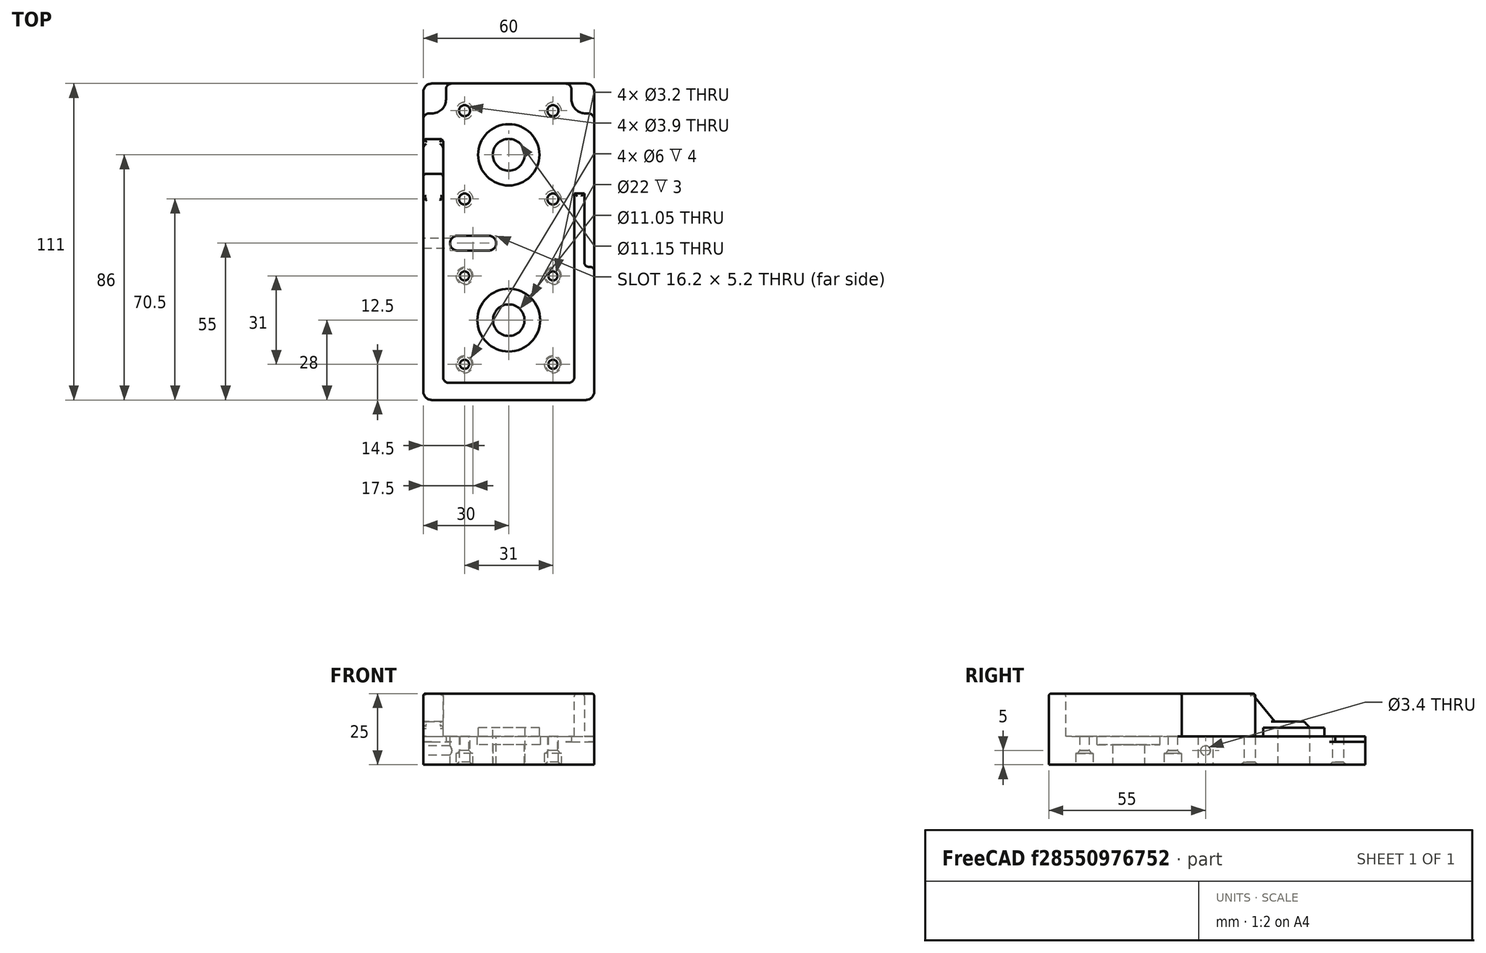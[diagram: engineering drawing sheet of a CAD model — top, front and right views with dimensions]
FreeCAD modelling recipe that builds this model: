
FCSTD DOCUMENT  (FreeCAD 0.19R)
Label: BeltDriveUnit2
License: All rights reserved
LicenseURL: http://en.wikipedia.org/wiki/All_rights_reserved
objects: Sketcher::SketchObject×11, PartDesign::Fillet×9, PartDesign::Pocket×8, PartDesign::Pad×3, PartDesign::Chamfer×3, PartDesign::Body×1, Mesh::Feature×1
note: 58 computed .brp shape members not serialized (recipe doc carries the construction recipe); baked Part::Feature solids carry a one-line shape summary decoded from their .brp

FEATURE [Sketcher::SketchObject] Sketch
  FullyConstrained = true
  MapMode = 5
  Support = -> [XY_Plane]
  sketch-geometry (17):
    g0: LineSegment StartX=-30 StartY=25 StartZ=0 EndX=30 EndY=25 EndZ=0
    g1: LineSegment StartX=30 StartY=25 StartZ=0 EndX=30 EndY=-86 EndZ=0
    g2: LineSegment StartX=30 StartY=-86 StartZ=0 EndX=-30 EndY=-86 EndZ=0
    g3: LineSegment StartX=-30 StartY=-86 StartZ=0 EndX=-30 EndY=25 EndZ=0
    g4: LineSegment StartX=-21 StartY=21 StartZ=0 EndX=21 EndY=21 EndZ=0
    g5: LineSegment StartX=21 StartY=21 StartZ=0 EndX=21 EndY=-21 EndZ=0
    g6: LineSegment StartX=21 StartY=-21 StartZ=0 EndX=-21 EndY=-21 EndZ=0
    g7: LineSegment StartX=-21 StartY=-21 StartZ=0 EndX=-21 EndY=21 EndZ=0
    g8: Circle CenterX=-15.5 CenterY=15.5 CenterZ=0 NormalX=0 NormalY=0 NormalZ=1 AngleXU=0 Radius=1.95
    g9: Circle CenterX=15.5 CenterY=15.5 CenterZ=0 NormalX=0 NormalY=0 NormalZ=1 AngleXU=0 Radius=1.95
    g10: Circle CenterX=-15.5 CenterY=-15.5 CenterZ=0 NormalX=0 NormalY=0 NormalZ=1 AngleXU=0 Radius=1.95
    g11: Circle CenterX=15.5 CenterY=-15.5 CenterZ=0 NormalX=0 NormalY=0 NormalZ=1 AngleXU=0 Radius=1.95
    g12: Circle CenterX=0 CenterY=-58 CenterZ=0 NormalX=0 NormalY=0 NormalZ=1 AngleXU=0 Radius=5.525
    g13: Circle CenterX=-15.5 CenterY=-42.5 CenterZ=0 NormalX=0 NormalY=0 NormalZ=1 AngleXU=0 Radius=1.6
    g14: Circle CenterX=15.5 CenterY=-42.5 CenterZ=0 NormalX=0 NormalY=0 NormalZ=1 AngleXU=0 Radius=1.6
    g15: Circle CenterX=-15.5 CenterY=-73.5 CenterZ=0 NormalX=0 NormalY=0 NormalZ=1 AngleXU=0 Radius=1.6
    g16: Circle CenterX=15.5 CenterY=-73.5 CenterZ=0 NormalX=0 NormalY=0 NormalZ=1 AngleXU=0 Radius=1.6
  constraints (44):
    c: Coincident(g0,g1)
    c: Coincident(g1,g2)
    c: Coincident(g2,g3)
    c: Coincident(g3,g0)
    c: Horizontal(g2)
    c: Vertical(g1)
    c: Vertical(g3)
    c: Coincident(g4,g5)
    c: Coincident(g5,g6)
    c: Coincident(g6,g7)
    c: Coincident(g7,g4)
    c: Horizontal(g4)
    c: Horizontal(g6)
    c: Vertical(g5)
    c: Vertical(g7)
    c: Equal(g5,g4)
    c: Distance(g5) = 42
    c: Symmetric(g4,g6,g-1)
    c: Symmetric(g0,g0,g-2)
    c: Distance(g4,g0) = 4
    c: Distance(g0) = 60
    c: Diameter(g11) = 3.9
    c: Equal(g11,g10)
    c: Equal(g11,g8)
    c: Equal(g11,g9)
    c: Distance(g9,g8) = 31
    c: Symmetric(g9,g8,g-2)
    c: Distance(g10,g8) = 31
    c: DistanceY(g11,g9) = 31
    c: DistanceX(g10,g11) = 31
    c: Symmetric(g9,g10,g-1)
    c: Diameter(g16) = 3.2
    c: Equal(g16,g14)
    c: Equal(g16,g13)
    c: Equal(g16,g15)
    c: Symmetric(g14,g13,g-2)
    c: Symmetric(g16,g15,g-2)
    c: Symmetric(g16,g13,g12)
    c: PointOnObject(g12,g-2)
    c: Distance(g14,g13) = 31
    c: Distance(g16,g14) = 31
    c: Distance(g-1,g12) = 58
    c: Diameter(g12) = 11.05
    c: DistanceY(g1) = -86
FEATURE [PartDesign::Pad] Pad
  Direction = (1,1,1)
  Length = 10
  Length2 = 100
  Profile = -> Sketch
  Type = 0
FEATURE [Sketcher::SketchObject] Sketch004
  FullyConstrained = true
  MapMode = 5
  Placement = pos=(0,0,10) rot=(0,0,1;0rad)
  Support = -> [Pad]
  sketch-geometry (1):
    g0: Circle CenterX=0 CenterY=0 CenterZ=0 NormalX=0 NormalY=0 NormalZ=1 AngleXU=0 Radius=10.75
  constraints (2):
    c: Coincident(g0,g-1)
    c: Diameter(g0) = 21.5
FEATURE [PartDesign::Pad] Pad001
  BaseFeature = -> Pad
  Direction = (1,1,1)
  Length = 3
  Length2 = 100
  Profile = -> Sketch004
  Type = 0
FEATURE [Sketcher::SketchObject] Sketch003
  FullyConstrained = false
  MapMode = 5
  Placement = pos=(0,0,13) rot=(0,0,1;0rad)
  Support = -> [Pad001]
  sketch-geometry (1):
    g0: Circle CenterX=0 CenterY=0 CenterZ=0 NormalX=0 NormalY=0 NormalZ=1 AngleXU=0 Radius=5.575
  constraints (1):
    c: Diameter(g0) = 11.15
FEATURE [PartDesign::Pocket] Pocket
  BaseFeature = -> Pad001
  Length = 5
  Length2 = 100
  Profile = -> Sketch003
  Type = 1
FEATURE [Sketcher::SketchObject] Sketch006
  ExternalGeometry = -> [Pocket]
  FullyConstrained = true
  MapMode = 5
  Placement = pos=(0,0,10) rot=(0,0,1;0rad)
  Support = -> [Pocket]
  sketch-geometry (1):
    g0: Circle CenterX=0 CenterY=-58 CenterZ=0 NormalX=0 NormalY=0 NormalZ=1 AngleXU=0 Radius=11
  constraints (2):
    c: Coincident(g0,g-3)
    c: Diameter(g0) = 22
FEATURE [PartDesign::Pocket] Pocket001
  BaseFeature = -> Pocket
  Length = 3
  Length2 = 100
  Profile = -> Sketch006
  Type = 0
FEATURE [Sketcher::SketchObject] Sketch007
  ExternalGeometry = -> [Pocket001]
  FullyConstrained = true
  MapMode = 5
  Placement = pos=(0,0,0) rot=(1,0,0;3.14159rad)
  Support = -> [Pocket001]
  sketch-geometry (4):
    g0: Circle CenterX=-15.5 CenterY=73.5 CenterZ=0 NormalX=0 NormalY=0 NormalZ=1 AngleXU=0 Radius=3
    g1: Circle CenterX=15.5 CenterY=73.5 CenterZ=0 NormalX=0 NormalY=0 NormalZ=1 AngleXU=0 Radius=3
    g2: Circle CenterX=15.5 CenterY=42.5 CenterZ=0 NormalX=0 NormalY=0 NormalZ=1 AngleXU=0 Radius=3
    g3: Circle CenterX=-15.5 CenterY=42.5 CenterZ=0 NormalX=0 NormalY=0 NormalZ=1 AngleXU=0 Radius=3
  constraints (9):
    c: Diameter(g3) = 6
    c: Equal(g3,g1)
    c: Equal(g3,g2)
    c: Equal(g3,g0)
    c: Symmetric(g0,g2,g-3)
    c: Symmetric(g1,g3,g-3)
    c: Distance(g2,g1) = 31
    c: Distance(g3,g2) = 31
    c: Symmetric(g3,g2,g-2)
FEATURE [PartDesign::Pocket] Pocket002
  BaseFeature = -> Pocket001
  Length = 4
  Length2 = 100
  Profile = -> Sketch007
  Type = 0
FEATURE [Sketcher::SketchObject] Sketch008  label="Slot"
  ExternalGeometry = -> [Pocket002]
  FullyConstrained = true
  MapMode = 5
  Placement = pos=(0,0,10) rot=(0,0,1;0rad)
  Support = -> [Pocket002]
  sketch-geometry (11):
    g0: Circle CenterX=0 CenterY=0 CenterZ=0 NormalX=0 NormalY=0 NormalZ=1 AngleXU=0 Radius=18.5
    g1: Circle CenterX=0 CenterY=-58 CenterZ=0 NormalX=0 NormalY=0 NormalZ=1 AngleXU=0 Radius=6
    g2: LineSegment StartX=-18.0653 StartY=-3.98707 StartZ=0 EndX=-5.859 EndY=-59.2931 EndZ=0
    g3: ArcOfCircle CenterX=-18 CenterY=-31 CenterZ=0 NormalX=0 NormalY=0 NormalZ=1 AngleXU=0 Radius=2.6 StartAngle=1.5708 EndAngle=4.71239
    g4: ArcOfCircle CenterX=-7 CenterY=-31 CenterZ=0 NormalX=0 NormalY=0 NormalZ=1 AngleXU=0 Radius=2.6 StartAngle=4.71239 EndAngle=7.85398
    g5: LineSegment StartX=-18 StartY=-33.6 StartZ=0 EndX=-7 EndY=-33.6 EndZ=0
    g6: LineSegment StartX=-18 StartY=-28.4 StartZ=0 EndX=-7 EndY=-28.4 EndZ=0
    g7: Circle CenterX=-18 CenterY=-31 CenterZ=0 NormalX=0 NormalY=0 NormalZ=1 AngleXU=0 Radius=6
    g8: Circle CenterX=-7 CenterY=-31 CenterZ=0 NormalX=0 NormalY=0 NormalZ=1 AngleXU=0 Radius=6
    g9: LineSegment StartX=-15.5 StartY=-37 StartZ=0 EndX=-15.5 EndY=-79 EndZ=0
    g10: LineSegment StartX=-15.5 StartY=-31 StartZ=0 EndX=-15.5 EndY=-37 EndZ=0
  constraints (29):
    c: Diameter(g0) = 37
    c: Coincident(g0,g-1)
    c: Diameter(g1) = 12
    c: Coincident(g1,g-3)
    c: PointOnObject(g2,g0)
    c: PointOnObject(g2,g1)
    c: Tangent(g2,g0)
    c: Tangent(g1,g2)
    c: Tangent(g3,g6) = 1.5708
    c: Tangent(g3,g5) = -1.5708
    c: Tangent(g5,g4) = -1.5708
    c: Tangent(g6,g4) = 1.5708
    c: Horizontal(g5)
    c: Equal(g3,g4)
    c: Diameter(g7) = 12
    c: Coincident(g3,g7)
    c: Diameter(g8) = 12
    c: Coincident(g8,g4)
    c: Distance(g3,g3) = 5.2
    c: Distance(g6) = 11
    c: DistanceX(g4) = -7
    c: Vertical(g9)
    c: Distance(g9) = 42
    c: PointOnObject(g-5,g9)
    c: DistanceY(g-5,g9) = 5.5
    c: Vertical(g10)
    c: Distance(g10) = 6
    c: Coincident(g10,g9)
    c: DistanceY(g10,g3) = 0
FEATURE [PartDesign::Pocket] Pocket003
  BaseFeature = -> Pocket002
  Length = 5
  Length2 = 100
  Profile = -> Sketch008
  Type = 1
FEATURE [Sketcher::SketchObject] Sketch009  label="JackScrew"
  FullyConstrained = true
  MapMode = 5
  Placement = pos=(-30,0,0) rot=(0.57735,-0.57735,-0.57735;2.0944rad)
  Support = -> [Pocket003]
  sketch-geometry (1):
    g0: Circle CenterX=31 CenterY=5 CenterZ=0 NormalX=0 NormalY=0 NormalZ=1 AngleXU=0 Radius=1.7
  constraints (3):
    c: Diameter(g0) = 3.4
    c: DistanceY(g0) = 5
    c: DistanceX(g0) = 31
FEATURE [PartDesign::Pocket] Pocket004
  BaseFeature = -> Pocket003
  Length = 12
  Length2 = 100
  Profile = -> Sketch009
  Type = 0
FEATURE [Sketcher::SketchObject] Sketch014  label="Stiffernerring"
  ExternalGeometry = -> [Pocket004]
  FullyConstrained = false
  MapMode = 5
  Placement = pos=(0,0,10) rot=(0,0,1;0rad)
  Support = -> [Pocket004]
  sketch-geometry (8):
    g0: LineSegment StartX=-30 StartY=5.5 StartZ=0 EndX=-23 EndY=5.5 EndZ=0
    g1: LineSegment StartX=-23 StartY=5.5 StartZ=0 EndX=-23 EndY=-80 EndZ=0
    g2: LineSegment StartX=-23 StartY=-80 StartZ=0 EndX=23 EndY=-80 EndZ=0
    g3: LineSegment StartX=23 StartY=-80 StartZ=0 EndX=23 EndY=-13.5 EndZ=0
    g4: LineSegment StartX=23 StartY=-13.5 StartZ=0 EndX=30 EndY=-13.5 EndZ=0
    g5: LineSegment StartX=30 StartY=-13.5 StartZ=0 EndX=30 EndY=-86 EndZ=0
    g6: LineSegment StartX=30 StartY=-86 StartZ=0 EndX=-30 EndY=-86 EndZ=0
    g7: LineSegment StartX=-30 StartY=-86 StartZ=0 EndX=-30 EndY=5.5 EndZ=0
  constraints (20):
    c: Coincident(g0,g1)
    c: Vertical(g1)
    c: Coincident(g1,g2)
    c: Horizontal(g2)
    c: Coincident(g2,g3)
    c: Vertical(g3)
    c: Coincident(g3,g4)
    c: Coincident(g4,g5)
    c: Coincident(g5,g6)
    c: Coincident(g6,g7)
    c: Coincident(g7,g0)
    c: Horizontal(g0)
    c: Distance(g0) = 7
    c: Horizontal(g4)
    c: Distance(g4) = 7
    c: Distance(g2,g6) = 6
    c: PointOnObject(g4,g-5)
    c: DistanceY(g-6,g0) = 21
    c: Coincident(g5,g-5)
    c: Coincident(g6,g-4)
FEATURE [PartDesign::Pad] Pad002
  BaseFeature = -> Pocket004
  Direction = (1,1,1)
  Length = 15
  Length2 = 100
  Profile = -> Sketch014
  Type = 0
FEATURE [Sketcher::SketchObject] Sketch016  label="RightReleif"
  FullyConstrained = false
  MapMode = 5
  Placement = pos=(0,0,25) rot=(0,0,1;0rad)
  Support = -> [Pad002]
  sketch-geometry (4):
    g0: LineSegment StartX=26.5 StartY=31.8178 StartZ=0 EndX=43.3193 EndY=31.8178 EndZ=0
    g1: LineSegment StartX=43.3193 StartY=31.8178 StartZ=0 EndX=43.3193 EndY=-39.2862 EndZ=0
    g2: LineSegment StartX=43.3193 StartY=-39.2862 StartZ=0 EndX=26.5 EndY=-39.2862 EndZ=0
    g3: LineSegment StartX=26.5 StartY=-39.2862 StartZ=0 EndX=26.5 EndY=31.8178 EndZ=0
  constraints (8):
    c: Coincident(g0,g1)
    c: Coincident(g1,g2)
    c: Coincident(g2,g3)
    c: Coincident(g3,g0)
    c: Horizontal(g0)
    c: Horizontal(g2)
    c: Vertical(g1)
    c: Vertical(g3)
FEATURE [PartDesign::Pocket] Pocket005
  BaseFeature = -> Pad002
  Length = 15
  Length2 = 100
  Profile = -> Sketch016
  Type = 0
FEATURE [Sketcher::SketchObject] Sketch017
  FullyConstrained = false
  MapMode = 5
  Placement = pos=(-30,0,0) rot=(0.57735,-0.57735,-0.57735;2.0944rad)
  Support = -> [Pocket005]
  sketch-geometry (4):
    g0: LineSegment StartX=-9.46299 StartY=15.1859 StartZ=0 EndX=6.67521 EndY=15.1859 EndZ=0
    g1: LineSegment StartX=6.67521 StartY=15.1859 StartZ=0 EndX=16.6576 EndY=27.3311 EndZ=0
    g2: LineSegment StartX=16.6576 StartY=27.3311 StartZ=0 EndX=-19.9445 EndY=30.3258 EndZ=0
    g3: LineSegment StartX=-19.9445 StartY=30.3258 StartZ=0 EndX=-9.46299 EndY=15.1859 EndZ=0
  constraints (5):
    c: Horizontal(g0)
    c: Coincident(g0,g1)
    c: Coincident(g1,g2)
    c: Coincident(g2,g3)
    c: Coincident(g3,g0)
FEATURE [PartDesign::Pocket] Pocket006
  BaseFeature = -> Pocket005
  Length = 9
  Length2 = 100
  Profile = -> Sketch017
  Type = 0
FEATURE [Sketcher::SketchObject] Sketch018
  FullyConstrained = false
  MapMode = 5
  Placement = pos=(0,0,10) rot=(0,0,1;0rad)
  Support = -> [Pocket006]
  sketch-geometry (10):
    g0: ArcOfCircle CenterX=27 CenterY=19.5 CenterZ=0 NormalX=0 NormalY=0 NormalZ=1 AngleXU=0 Radius=5 StartAngle=3.14159 EndAngle=4.71239
    g1: ArcOfCircle CenterX=-27 CenterY=19.5 CenterZ=0 NormalX=0 NormalY=0 NormalZ=1 AngleXU=0 Radius=5 StartAngle=4.71239 EndAngle=6.28319
    g2: LineSegment StartX=27 StartY=14.5 StartZ=0 EndX=39.22 EndY=14.5 EndZ=0
    g3: LineSegment StartX=39.22 StartY=14.5 StartZ=0 EndX=39.22 EndY=33.52 EndZ=0
    g4: LineSegment StartX=39.22 StartY=33.52 StartZ=0 EndX=22 EndY=33.52 EndZ=0
    g5: LineSegment StartX=22 StartY=33.52 StartZ=0 EndX=22 EndY=19.5 EndZ=0
    g6: LineSegment StartX=-22 StartY=19.5 StartZ=0 EndX=-22 EndY=33.52 EndZ=0
    g7: LineSegment StartX=-22 StartY=33.52 StartZ=0 EndX=-39.22 EndY=33.52 EndZ=0
    g8: LineSegment StartX=-39.22 StartY=33.52 StartZ=0 EndX=-39.22 EndY=14.5 EndZ=0
    g9: LineSegment StartX=-39.22 StartY=14.5 StartZ=0 EndX=-27 EndY=14.5 EndZ=0
  constraints (25):
    c: DistanceX(g0) = 27
    c: Symmetric(g0,g1,g-2)
    c: Horizontal(g2)
    c: Coincident(g2,g3)
    c: Vertical(g3)
    c: Coincident(g3,g4)
    c: Horizontal(g4)
    c: Coincident(g4,g5)
    c: Vertical(g5)
    c: Tangent(g1,g6) = -1.5708
    c: Coincident(g6,g7)
    c: Horizontal(g7)
    c: Coincident(g7,g8)
    c: Coincident(g8,g9)
    c: Horizontal(g9)
    c: Vertical(g6)
    c: Tangent(g2,g0) = -1.5708
    c: Tangent(g5,g0) = -1.5708
    c: Tangent(g9,g1) = -1.5708
    c: Vertical(g8)
    c: Symmetric(g3,g7,g-2)
    c: DistanceY(g4) = 33.52
    c: DistanceX(g3) = 39.22
    c: Diameter(g0) = 10
    c: Diameter(g1) = 10
FEATURE [PartDesign::Pocket] Pocket007
  BaseFeature = -> Pocket006
  Length = 2
  Length2 = 100
  Profile = -> Sketch018
  Type = 0
FEATURE [PartDesign::Chamfer] Chamfer
  Angle = 45
  Base = -> Pocket007 [Edge103]
  BaseFeature = -> Pocket007
  ChamferType = 0
  FlipDirection = false
  Size = 2
  Size2 = 1
  SupportTransform = false
FEATURE [PartDesign::Fillet] Fillet
  Base = -> Chamfer [Edge69,Edge65,Edge40,Edge109]
  BaseFeature = -> Chamfer
  Radius = 3
  SupportTransform = false
FEATURE [PartDesign::Fillet] Fillet001
  Base = -> Fillet [Edge13,Edge107]
  BaseFeature = -> Fillet
  Radius = 2
  SupportTransform = false
FEATURE [PartDesign::Fillet] Fillet002
  Base = -> Fillet001 [Edge80,Edge144]
  BaseFeature = -> Fillet001
  Radius = 2
  SupportTransform = false
FEATURE [PartDesign::Fillet] Fillet003
  Base = -> Fillet002 [Edge77,Edge75]
  BaseFeature = -> Fillet002
  Radius = 1
  SupportTransform = false
FEATURE [PartDesign::Fillet] Fillet004
  Base = -> Fillet003 [Face35]
  BaseFeature = -> Fillet003
  Radius = 1
  SupportTransform = false
FEATURE [PartDesign::Fillet] Fillet005
  Base = -> Fillet004 [Edge136,Edge46]
  BaseFeature = -> Fillet004
  Radius = 1
  SupportTransform = false
FEATURE [PartDesign::Fillet] Fillet006
  Base = -> Fillet005 [Edge86,Edge87]
  BaseFeature = -> Fillet005
  Radius = 1.5
  SupportTransform = false
FEATURE [PartDesign::Fillet] Fillet007
  Base = -> Fillet006 [Edge49,Edge45]
  BaseFeature = -> Fillet006
  Radius = 2
  SupportTransform = false
FEATURE [PartDesign::Fillet] Fillet008
  Base = -> Fillet007 [Face1]
  BaseFeature = -> Fillet007
  Radius = 1
  SupportTransform = false
FEATURE [PartDesign::Chamfer] Chamfer001
  Angle = 45
  Base = -> Fillet008 [Edge231,Edge229,Edge223,Edge225]
  BaseFeature = -> Fillet008
  ChamferType = 0
  FlipDirection = false
  Size = 1
  Size2 = 1
  SupportTransform = false
FEATURE [PartDesign::Chamfer] Chamfer002
  Angle = 45
  Base = -> Chamfer001 [Edge127,Edge129,Edge121,Edge125]
  BaseFeature = -> Chamfer001
  ChamferType = 0
  FlipDirection = false
  Size = 1
  Size2 = 1
  SupportTransform = false
FEATURE [PartDesign::Body] Body
  Group = -> [Sketch,Pad,Sketch003,Sketch004,Pad001,Pocket,Sketch006,Pocket001,Sketch007,Pocket002,Sketch008,Pocket003,Sketch009,Pocket004,Sketch014,Sketch016,Pad002,Sketch017,Sketch018,Pocket005,Pocket006,Pocket007,Chamfer,Fillet,Fillet001,Fillet002,Fillet003,Fillet004,Fillet005,Fillet006,Fillet007,Fillet008,Chamfer001,Chamfer002]
  Origin = -> Origin
  Tip = -> Chamfer002
FEATURE [Mesh::Feature] Mesh  label="Chamfer002 (Meshed)"
